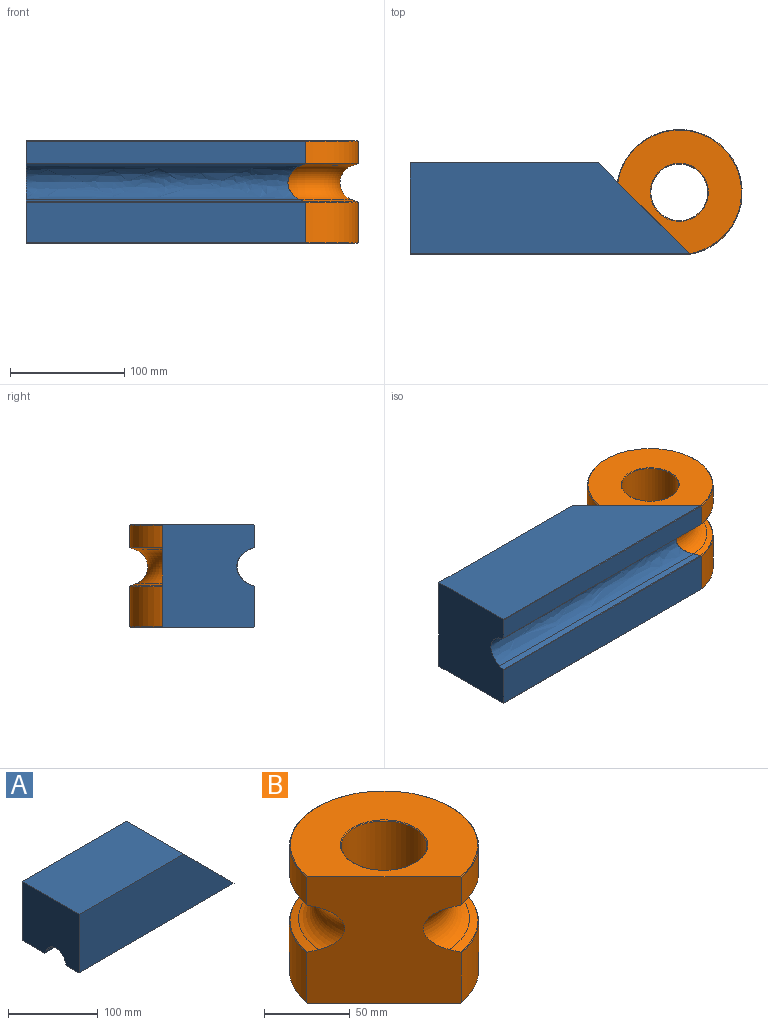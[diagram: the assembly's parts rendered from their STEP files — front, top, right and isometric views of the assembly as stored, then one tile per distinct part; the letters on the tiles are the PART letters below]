
ASSEMBLY  parts=2 mates=1
PART A: 14 faces, bbox 245x90x80 mm
  f0: plane 245x35.3mm, normal (0,0,-1), area 8647.4mm2, adj f1,f6,f7,f12
  f1: plane 90x80mm, normal (0.71,0,0.71), area 9639.5mm2, adj f0,f2,f3,f4,f5,f7,f8,f9
  f2: plane 165x90mm, normal (0,0,1), area 14850mm2, adj f1,f3,f4,f6
  f3: plane 244.5x79.5mm, normal (0,-1,0), area 16277.6mm2, adj f1,f2,f6,f8
  f4: plane 244.5x79.5mm, normal (0,1,0), area 16277.6mm2, adj f1,f2,f6,f7
  f5: plane 245x19.3mm, normal (0,0,-1), area 4727.4mm2, adj f1,f6,f8,f11
  f6: plane 90x80mm, normal (-1,0,0), area 6816.2mm2, adj f0,f2,f3,f4,f5,f7,f8,f9
  f7: plane 245x0.5mm, normal (0,0.71,-0.71), area 173.1mm2, adj f0,f1,f4,f6
  f8: plane 245x0.5mm, normal (0,-0.71,-0.71), area 173.1mm2, adj f1,f3,f5,f6
  f9: extruded ~240.31x30.01mm, area 9169.9mm2, adj f1,f6,f10,f13
  f10: extruded ~244.71x4.4mm, area 1146.8mm2, adj f1,f6,f9,f11
  f11: extruded ~245x0.47mm, area 135.7mm2, adj f1,f5,f6,f10
  f12: extruded ~245x0.47mm, area 135.7mm2, adj f0,f1,f6,f13
  f13: extruded ~244.71x4.4mm, area 1146.8mm2, adj f1,f6,f9,f12
PART B: 15 faces, bbox 119.3x119.3x90.2 mm
  f0: plane 108.29x108.29mm, normal (0,0,1), area 5898.6mm2, adj f8,f13,f14
  f1: cylinder r=55mm len=109.22mm, axis (0,0,-1), area 4643.5mm2, adj f8,f12,f13
  f2: cylinder r=24.9mm len=89mm, axis (0,0,-1), area 13924.2mm2, adj f9,f14
  f3: cylinder r=55mm len=109.22mm, axis (0,0,-1), area 8493.9mm2, adj f8,f10,f11
  f4: plane 108.29x108.29mm, normal (0,0,-1), area 5898.6mm2, adj f8,f9,f10
  f5: cone r=55mm half-angle=70.7deg, axis (0,0,-1), area 1215mm2, adj f6,f8,f11
  f6: torus R=55mm, axis (0,0,1), area 8103.4mm2, adj f5,f7,f8
  f7: cone r=55mm half-angle=70.7deg, axis (0,0,1), area 1215mm2, adj f6,f8,f12
  f8: plane 90.2x63.64mm, normal (-0.71,-0.71,0), area 6989.4mm2, adj f0,f1,f3,f4,f5,f6,f7,f10
  f9: cone r=25.4mm half-angle=45deg, axis (0,0,-1), area 111.7mm2, adj f2,f4
  f10: cone r=55mm half-angle=45deg, axis (0,0,1), area 169.6mm2, adj f3,f4,f8
  f11: cone r=54.67mm half-angle=35.3deg, axis (0,0,-1), area 138.9mm2, adj f3,f5,f8
  f12: cone r=55mm half-angle=35.3deg, axis (0,0,1), area 138.9mm2, adj f1,f7,f8
  f13: cone r=54.5mm half-angle=45deg, axis (0,0,-1), area 169.6mm2, adj f0,f1,f8
  f14: cone r=24.9mm half-angle=45deg, axis (0,0,1), area 111.7mm2, adj f0,f2
PLACE A rot(axis=(-1,0,0),90deg) t=(-234.26,-28.33,-7.48)mm
PLACE B t=(1.52,25.89,-7.48)mm fixed
MATE fastened A.f1 <-> B.f8  axis (0.71,0.71,0) through (10.74,-28.33,82.02)mm
